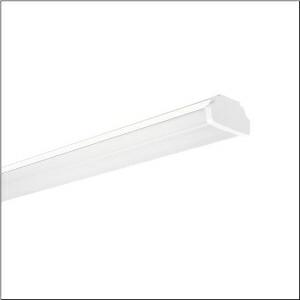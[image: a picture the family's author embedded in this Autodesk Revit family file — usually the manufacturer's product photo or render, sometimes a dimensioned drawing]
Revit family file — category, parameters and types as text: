
# Revit family: modario_r__31_gen_2_53bm812cv675c2_0c1f
name_source: partatom
category: Lighting Fixtures
units: mm (PartAtom-declared; Revit-internal decimal feet)

## family parameters
Cut with Voids When Loaded = No
Host = Face
Light Source = No
Part Type = Normal
Room Calculation Point = No
Round Connector Dimension = Use Diameter
Shared = No

## types (1)
- --- (1 x LED, 7670 lm, 42.1 W, 6500K)
    Apparent Load = 42 VA
    CIE Flux Codes = 47 80 95 93 100
    Color Rendering = 80
    Color Temperature = 6500K
    Default Elevation = 1800 mm
    Description = Modario® 31 Gen.2, luminaire insert, of sheet steel, coil coated, white, length: 1.495mm, width: 81mm, height: 82mm, 5x system unit, system units: 299mm, LED rated luminous flux: 7.670lm, light colour: 865, control gear: ON/OFF Multilumen, CLOi, with plug, 3-pole, with phase selection, mains connection: 220..240V, AC, 50/60Hz, start of lifetime: 42W, end of service life: 50W, through-wiring accessed according to module size, primary optical cover: cover, of PMMA, light emission: direct distribution, primary light characteristic: symmetric, protection rating (complete): IP20, protection rating (LED compartment): IP50, insulation class (complete): insulation class I (protective earthing), certification: CE, ENEC, VDE, UKCA, impact resistance: IK03, permissible ambient temperature for indoor applications: -35..+50°C, corresponds to IFS (International Featured Standards) requirements for safety and quality in the food industry, reducing of maximum allowable ambient temperature of 5°C with ceiling mounting, IP40 when using the optional accessory 5TP9018, packaging unit: 1 piece
    Height = 92 mm
    Lamp = 1 x LED
    Lamp Light Flux = 7670 lm
    Lamp Power = 42.1 W
    Lamp count = 1
    Length = 1495 mm
    Luminous efficacy = 182 lm/W
    Manufacturer = Siteco
    ModVariant = No
    Model = 53BM812CV675C2
    Mounting Place = Ceiling
    Mounting Type = Pendant
    Number of Poles = 1
    OnlyDefault = Yes
    Power Factor = 1
    Product Name = Modario® 31 Gen.2
    Product group = luminaire insert | ceiling pendant
    ProductGroupID = 902
    Protection Class = Protection class I
    Protection Degree = IP 20
    RLX_Detail_Level = 1
    RLX_Emergency_Light_Flux = 0 lm
    RLX_Emergency_Type = 0
    RLX_Emergency_Type_DB = No
    RlxData = <blob elided: 39949 chars, md5=ab898a61>
    Socket = socket
    Standby Power = 0 W
    System Light Flux = 7670 lm
    System Power = 42 W
    Type Comments = factory setting: luminous flux: 100 % | (A | C | E) | 98 mA
    Type Image = l_1341886.jpg
    URL = http://relux.com
    VarID = @adj_054121
    Voltage = 0 V
    Weight = 0.00 kg
    Width = 81 mm

## geometry (parser evidence)
native form markers: Blend x4, Sweep x11
no freeform markers — native parametric forms only
